# Revit family: Clevertronics_LUBPRO-D2-AUA01211530001
name_source: partatom
category: Lighting Fixtures
units: mm (PartAtom-declared; Revit-internal decimal feet)

## family parameters
Cut with Voids When Loaded = No
Host = Face
Light Source = Yes
Part Type = Normal
Room Calculation Point = No
Round Connector Dimension = Use Diameter
Shared = No

## types (5) — shared parameters
Apparent Load = 4 VA
Clevertronics_AS2293 Classification = C0=E6.3 C90=E6.3
Clevertronics_Battery = 3.3V 2500mAh
Clevertronics_Battery Type = Lithium Nanophosphate
Clevertronics_Charger Method = Intelligent current limited constant voltage
Clevertronics_Construction = PC/ABS Body with PC Diffuser
Clevertronics_Dimensions LED Enclosure = 317mm x 157mm x 8.7mm (Blade Assembly)
Clevertronics_Dimensions Main Enclosure = 385mm x 67mm x 80mm (Cover Plate)
Clevertronics_Height = 157 mm  [stored 0.515092 ft]
Clevertronics_Height Base = 67 mm
Clevertronics_IP Rating = IP20
Clevertronics_Length = 317 mm  [stored 1.04003 ft]
Clevertronics_Length Base = 385 mm  [stored 1.26312 ft]
Clevertronics_MIC Number = AUA01211530001
Clevertronics_Material = Clevertronics_Plastic
Clevertronics_Mounting = Recessed ceiling
Clevertronics_Operating Mode = Maintained
Clevertronics_Operating Temperature = 1˚C to 40˚C
Clevertronics_Operating Voltage = 240V AC; 50Hz
Clevertronics_Power Consumption = 4.2 Watts (Standby), 3.8 Watts (Max)
Clevertronics_Product Description = L10 Lithium Nanophosphate Ultrablade Pro Blade Exit, DALI-2
Clevertronics_Replacement Battery = 1530050
Clevertronics_Replacement Driver = AUM01270570001
Clevertronics_Replacement Lamp = 8002178
Clevertronics_Testing Node = 8003062
Clevertronics_Testing System = DALI-2
Clevertronics_Viewing Distance = 24M
Clevertronics_Weight = 1.1kg
Clevertronics_Width = 9 mm  [stored 0.0295276 ft]
Clevertronics_Width Base = 48 mm  [stored 0.15748 ft]
Color Filter = 16777215
Default Elevation = 1200 mm
Description = L10 Lithium Nanophosphate Ultrablade Pro Blade Exit, DALI-2
Dimming Lamp Color Temperature Shift = <None>
Indication Right 'Face Two' = No
Lamp = 12 x Duris E3 LED, 100,000 hours
Manufacturer = Clevertronics
Model = LUBPRO-D2
Tilt Angle = -90.00°
zero-valued in all types: Clevertronics_Annotation Size

## per-type parameters (varying)
| type | Indication Left 'Face Two' | Indication Left 'Face one' | Indication Right 'Face one' | Photometric Web File | Runing Man common arrow | Straight line 'Face one' | Straight line 'Face two' |
| Runing Man Single | No | No | No | CUBPRO_IESA_E_CIE_LL21009_20180522.IES | No | Yes | No |
| Running Man Common arrow | Yes | No | No | CUBPRO_IESA_E_CIE_LL21009_20180522.IES | Yes | No | No |
| Runing Man Right (Single) | No | No | Yes | CUBPRO_IESA_E_CIE_LL21009_20180522.IES | No | No | No |
| Runing Man Double Sided | No | No | No |  | No | Yes | Yes |
| Runing Man Left (Single) | No | Yes | No | CUBPRO_IESA_E_CIE_LL21009_20180522.IES | No | No | No |

note: [stored X ft] marks values corroborated as IEEE doubles in the binary element streams (Revit-internal decimal feet)

## geometry (parser evidence)
native form markers: Blend x2, Sweep x4
no freeform markers — native parametric forms only
